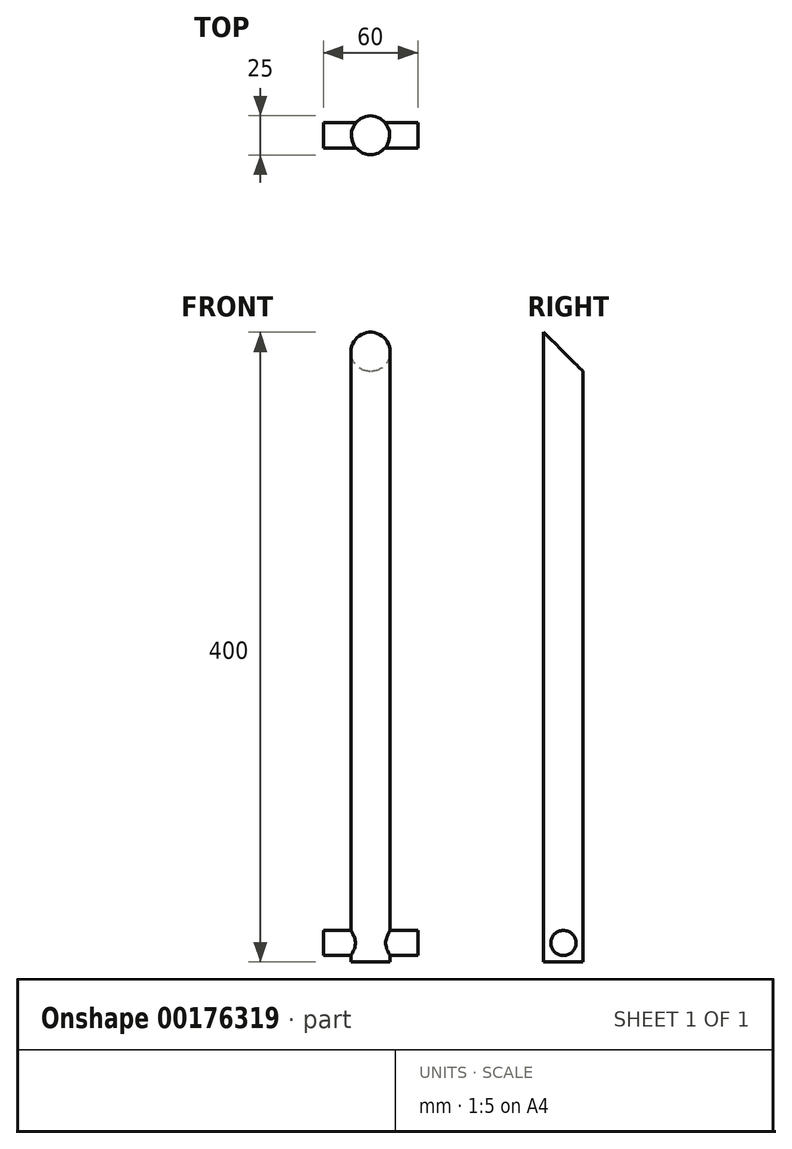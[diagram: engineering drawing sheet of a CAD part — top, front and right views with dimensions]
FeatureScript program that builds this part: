
annotation { "Feature Type Name" : "Feature", "Feature Type Description" : "" }
export const myFeature = defineFeature(function(context is Context, id is Id, definition is map)
    precondition{}
    {
        {
            var Q0;
            Q0=qCreatedBy(makeId("Top.planeOp"),FACE);
            var sketch = newSketch(context, id + "F0", { "sketchPlane" : qUnion([Q0])});
            skCircle(sketch, "E0", {"center": v(0, 0) * mm, "radius": 12.5 * mm});
            skSolve(sketch);
        }
        {
            var Q0;
            Q0=makeQuery(id+"F0.imprint","IMPRINT",FACE,{"disambiguationData":[TD([[makeQuery(id+"F0.imprint","IMPRINT",EDGE,{"derivedFrom":sQuery(id+"F0.wireOp",EDGE,"E0")}),1.0]])]});
            extrude(context, id + "F1", {"entities" : qUnion([Q0]), "depth" : 400 * mm});
        }
        {
            var Q0;
            Q0=qCreatedBy(makeId("Right.planeOp"),FACE);
            var sketch = newSketch(context, id + "F2", { "sketchPlane" : qUnion([Q0])});
            skCircle(sketch, "E1", {"center": v(0, 12) * mm, "radius": 8 * mm});
            skLineSegment(sketch, "E2", {"start": v(0, 0) * mm, "end": v(0, 12) * mm, "construction": true});
            skSolve(sketch);
        }
        {
            var Q0;
            Q0 = qSketchRegion(id + "F2", true);
            extrude(context, id + "F3", {"entities" : qUnion([Q0]), "operationType" : NewBodyOperationType.ADD, "endBound" : BoundingType.SYMMETRIC, "depth" : 60 * mm});
        }
        {
            var Q0;
            Q0=qCreatedBy(makeId("Right.planeOp"),FACE);
            var sketch = newSketch(context, id + "F4", { "sketchPlane" : qUnion([Q0])});
            skLineSegment(sketch, "E3.0", {"start": v(-12.5, 400) * mm, "end": v(12.5, 400) * mm});
            skLineSegment(sketch, "E4", {"start": v(12.5, 400) * mm, "end": v(12.5, 375) * mm});
            skLineSegment(sketch, "E5", {"start": v(12.5, 375) * mm, "end": v(-12.5, 400) * mm});
            skSolve(sketch);
        }
        {
            var Q0;
            Q0 = qSketchRegion(id + "F4", true);
            extrude(context, id + "F5", {"entities" : qUnion([Q0]), "operationType" : NewBodyOperationType.REMOVE, "endBound" : BoundingType.THROUGH_ALL, "oppositeDirection" : true, "depth" : 25 * mm, "hasSecondDirection" : true, "secondDirectionBound" : SecondDirectionBoundingType.THROUGH_ALL, "secondDirectionOppositeDirection" : false, "secondDirectionDepth" : 25 * mm});
        }
    });
